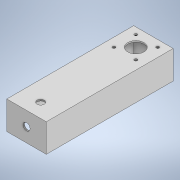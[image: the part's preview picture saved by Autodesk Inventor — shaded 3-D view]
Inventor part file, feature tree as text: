
AUTODESK INVENTOR PART (.ipt)
format: ipt  version: 2020 (Build 240168000, 168)  size: 149,504 bytes
history: native  units: mm
features: extrude x4, sketch x4, shell x1
ambient origin geometry x8: Origin, YZ Plane, XZ Plane, XY Plane, X Axis, Y Axis, Z Axis, Center Point
bodies: Body1 (feature_tree)
feature tree (9):
  extrude  "Extrusion1"  Depth=40.0mm
  shell  "Shell1"  Thickness=180.0mm
  extrude  "Extrusion2"  Depth=10.0mm
  extrude  "Extrusion3"  Depth=40.0mm
  extrude  "Extrusion4"  Depth=2.0mm
  sketch  "Sketch1"  dims[d1=56.0mm d2=40.0mm d3=180.0mm d4=0.0mm]
  sketch  "Sketch2"  dims[d5=2.0mm d6=10.0mm]
  sketch  "Sketch3"  dims[d7=180.0mm d8=0.0mm d9=40.0mm]
  sketch  "Sketch4"  dims[d10=4.0mm d11=23.0mm d12=115.0mm d13=31.0mm d14=2.0mm d15=0.0mm d16=10.0mm d17=10.0mm d18=2.0mm d19=0.0mm]
